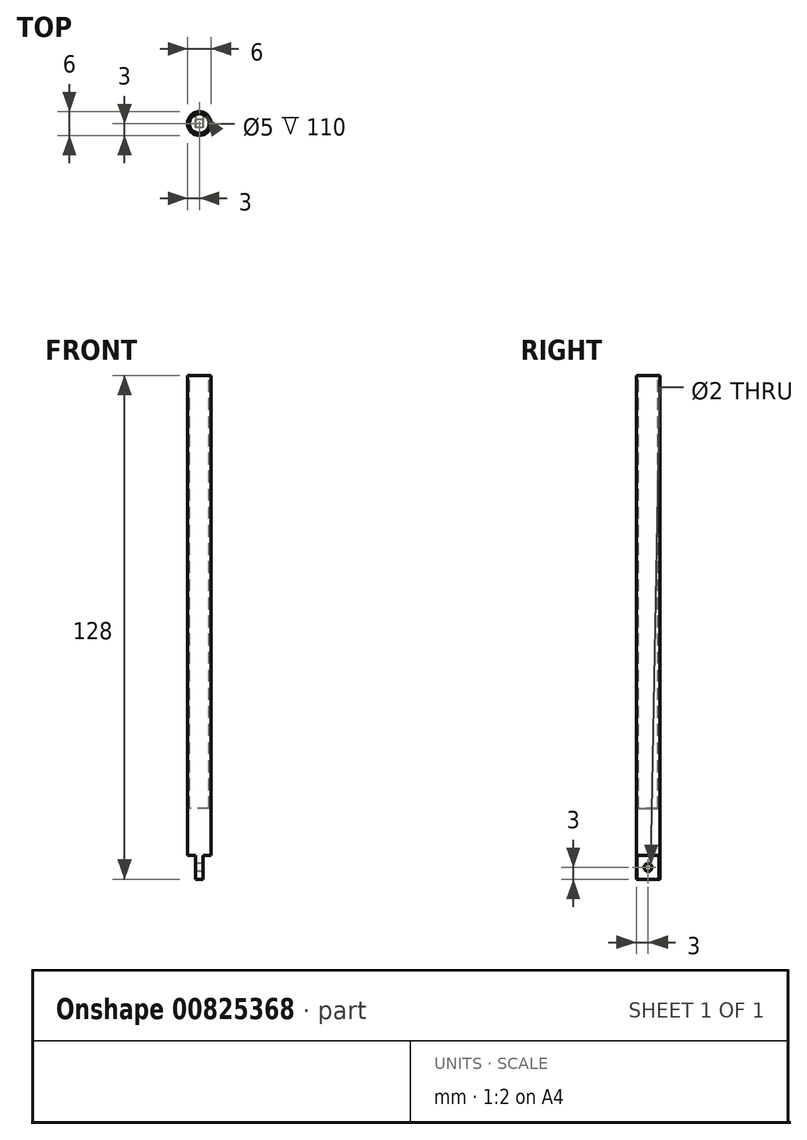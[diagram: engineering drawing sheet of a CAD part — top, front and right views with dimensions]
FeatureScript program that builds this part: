
annotation { "Feature Type Name" : "Feature", "Feature Type Description" : "" }
export const myFeature = defineFeature(function(context is Context, id is Id, definition is map)
    precondition{}
    {
        {
            var Q0;
            Q0=qCreatedBy(makeId("Top.planeOp"),FACE);
            var sketch = newSketch(context, id + "F0", { "sketchPlane" : qUnion([Q0])});
            skCircle(sketch, "E0", {"center": v(0, 0) * mm, "radius": 3 * mm});
            skSolve(sketch);
        }
        {
            var Q0;
            Q0 = qSketchRegion(id + "F0", true);
            extrude(context, id + "F1", {"entities" : qUnion([Q0]), "oppositeDirection" : true, "depth" : 128 * mm, "offsetDistance" : 25 * mm});
        }
        {
            var Q0;
            Q0=makeQuery(id+"F1.opExtrude","CAP_FACE",FACE,{"disambiguationData":[OSD([sQuery(id+"F0.wireOp",EDGE,"E0")])],"isStart":true});
            var sketch = newSketch(context, id + "F2", { "sketchPlane" : qUnion([Q0])});
            skCircle(sketch, "E1", {"center": v(0, 0) * mm, "radius": 2.5 * mm});
            skSolve(sketch);
        }
        {
            var Q0;
            Q0 = qSketchRegion(id + "F2", true);
            extrude(context, id + "F3", {"entities" : qUnion([Q0]), "operationType" : NewBodyOperationType.REMOVE, "oppositeDirection" : true, "depth" : 110 * mm, "offsetDistance" : 25 * mm});
        }
        {
            var Q0;
            Q0=qCreatedBy(makeId("Front.planeOp"),FACE);
            var sketch = newSketch(context, id + "F4", { "sketchPlane" : qUnion([Q0])});
            skLineSegment(sketch, "E2", {"start": v(0, 0) * mm, "end": v(0, -125) * mm, "construction": true});
            skLineSegment(sketch, "E3", {"start": v(0, -125) * mm, "end": v(0, -122) * mm, "construction": true});
            skLineSegment(sketch, "E4", {"start": v(0, -122) * mm, "end": v(1, -122) * mm, "construction": true});
            skLineSegment(sketch, "E5", {"start": v(0, -122) * mm, "end": v(-1, -122) * mm, "construction": true});
            skLineSegment(sketch, "E6.bottom", {"start": v(1, -122) * mm, "end": v(4.29, -122) * mm});
            skLineSegment(sketch, "E6.top", {"start": v(1, -128.8) * mm, "end": v(4.29, -128.8) * mm});
            skLineSegment(sketch, "E6.left", {"start": v(1, -122) * mm, "end": v(1, -128.8) * mm});
            skLineSegment(sketch, "E6.right", {"start": v(4.29, -122) * mm, "end": v(4.29, -128.8) * mm});
            skLineSegment(sketch, "E7.bottom", {"start": v(-1, -122) * mm, "end": v(-4.7, -122) * mm});
            skLineSegment(sketch, "E7.top", {"start": v(-1, -128.85) * mm, "end": v(-4.7, -128.85) * mm});
            skLineSegment(sketch, "E7.left", {"start": v(-1, -122) * mm, "end": v(-1, -128.85) * mm});
            skLineSegment(sketch, "E7.right", {"start": v(-4.7, -122) * mm, "end": v(-4.7, -128.85) * mm});
            skSolve(sketch);
        }
        {
            var Q0;
            Q0 = qSketchRegion(id + "F4", true);
            extrude(context, id + "F5", {"entities" : qUnion([Q0]), "operationType" : NewBodyOperationType.REMOVE, "endBound" : BoundingType.SYMMETRIC, "oppositeDirection" : true, "depth" : 25 * mm, "offsetDistance" : 25 * mm});
        }
        {
            var Q0;
            Q0=makeQuery(id+"F5.boolean.opBoolean","COPY",FACE,{"derivedFrom":makeQuery(id+"F5.opExtrude","SWEPT_FACE",FACE,{"disambiguationData":[OSD([sQuery(id+"F4.wireOp",EDGE,"E7.left")])]})});
            var sketch = newSketch(context, id + "F6", { "sketchPlane" : qUnion([Q0])});
            skLineSegment(sketch, "E8", {"start": v(0, -128) * mm, "end": v(0, -125) * mm, "construction": true});
            skCircle(sketch, "E9", {"center": v(0, -125) * mm, "radius": 1 * mm});
            skSolve(sketch);
        }
        {
            var Q0;
            Q0 = qSketchRegion(id + "F6", true);
            extrude(context, id + "F7", {"entities" : qUnion([Q0]), "operationType" : NewBodyOperationType.REMOVE, "oppositeDirection" : true, "depth" : 25 * mm, "offsetDistance" : 25 * mm});
        }
    });
